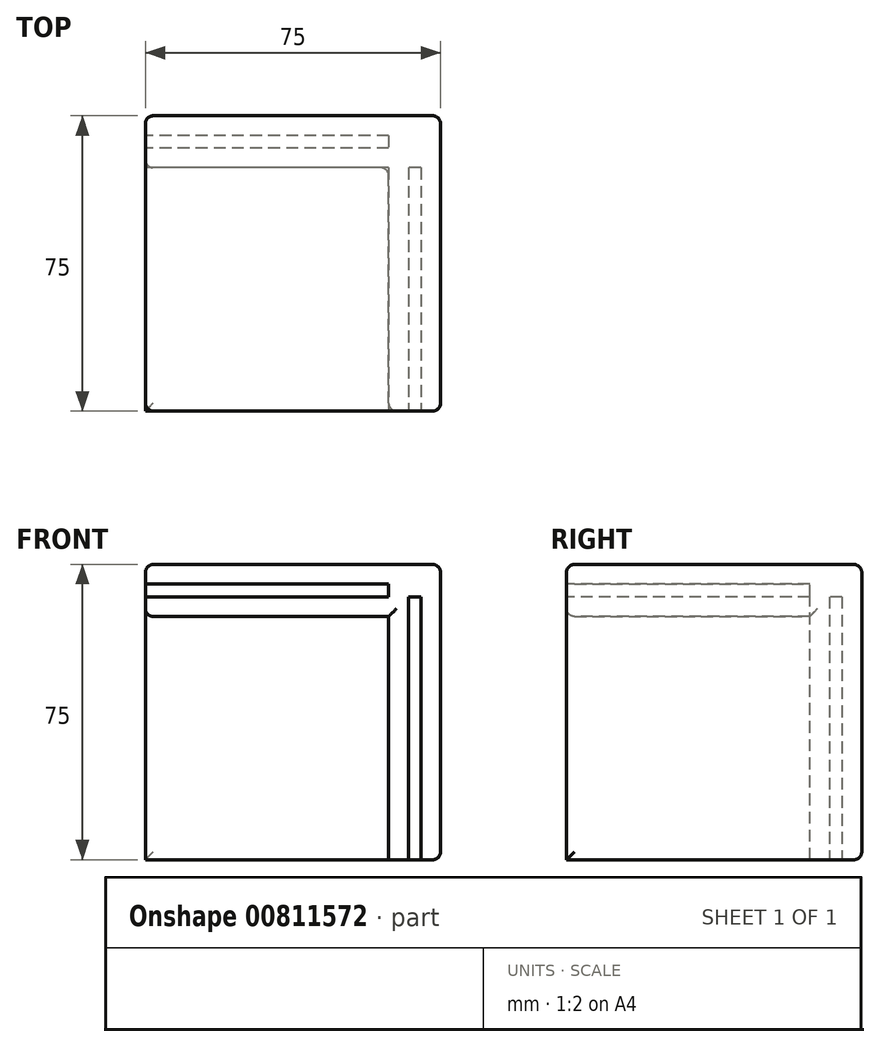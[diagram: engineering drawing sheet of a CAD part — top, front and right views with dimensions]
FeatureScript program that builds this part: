
annotation { "Feature Type Name" : "Feature", "Feature Type Description" : "" }
export const myFeature = defineFeature(function(context is Context, id is Id, definition is map)
    precondition{}
    {
        {
            var Q0;
            Q0=qCreatedBy(makeId("Top.planeOp"),FACE);
            var sketch = newSketch(context, id + "F0", { "sketchPlane" : qUnion([Q0])});
            skLineSegment(sketch, "E0.bottom", {"start": v(37.5, -37.5) * mm, "end": v(-37.5, -37.5) * mm});
            skLineSegment(sketch, "E0.top", {"start": v(37.5, 37.5) * mm, "end": v(-37.5, 37.5) * mm});
            skLineSegment(sketch, "E0.left", {"start": v(37.5, -37.5) * mm, "end": v(37.5, 37.5) * mm});
            skLineSegment(sketch, "E0.right", {"start": v(-37.5, -37.5) * mm, "end": v(-37.5, 37.5) * mm});
            skPoint(sketch, "E0.middle", {"position": v(0, 0) * mm});
            skSolve(sketch);
        }
        {
            var Q0;
            Q0=makeQuery(id+"F0.imprint","IMPRINT",FACE,{"disambiguationData":[TD([[makeQuery(id+"F0.imprint","IMPRINT",EDGE,{"derivedFrom":sQuery(id+"F0.wireOp",EDGE,"E0.bottom")}),-1.0]])]});
            extrude(context, id + "F1", {"entities" : qUnion([Q0]), "depth" : 5 * mm, "offsetDistance" : 25 * mm});
        }
        {
            var Q0;
            Q0=makeQuery(id+"F1.opExtrude","SWEPT_FACE",FACE,{"disambiguationData":[OSD([sQuery(id+"F0.wireOp",EDGE,"E0.right")])]});
            var sketch = newSketch(context, id + "F2", { "sketchPlane" : qUnion([Q0])});
            skLineSegment(sketch, "E1.bottom", {"start": v(-37.5, 5) * mm, "end": v(-32.5, 5) * mm});
            skLineSegment(sketch, "E1.top", {"start": v(-37.5, -70) * mm, "end": v(-32.5, -70) * mm});
            skLineSegment(sketch, "E1.left", {"start": v(-37.5, 5) * mm, "end": v(-37.5, -70) * mm});
            skLineSegment(sketch, "E1.right", {"start": v(-32.5, 5) * mm, "end": v(-32.5, -70) * mm});
            skLineSegment(sketch, "E2.bottom", {"start": v(-29.3, 5) * mm, "end": v(-24.3, 5) * mm});
            skLineSegment(sketch, "E2.top", {"start": v(-29.3, -70) * mm, "end": v(-24.3, -70) * mm});
            skLineSegment(sketch, "E2.left", {"start": v(-29.3, 5) * mm, "end": v(-29.3, -70) * mm});
            skLineSegment(sketch, "E2.right", {"start": v(-24.3, 5) * mm, "end": v(-24.3, -70) * mm});
            skSolve(sketch);
        }
        {
            var Q0;
            {var subQ0=sQuery(id+"F2.wireOp",EDGE,"E1.bottom");Q0=makeQuery(id+"F2.imprint","IMPRINT",FACE,{"disambiguationData":[TD([[makeQuery(id+"F2.imprint","IMPRINT",EDGE,{"derivedFrom":subQ0}),1.0]])]});}
            var Q1;
            {var subQ0=sQuery(id+"F2.wireOp",EDGE,"E2.bottom");Q1=makeQuery(id+"F2.imprint","IMPRINT",FACE,{"disambiguationData":[TD([[makeQuery(id+"F2.imprint","IMPRINT",EDGE,{"derivedFrom":subQ0}),1.0]])]});}
            var Q2;
            {var subQ0=sQuery(id+"F2.wireOp",EDGE,"E2.top");Q2=makeQuery(id+"F2.imprint","IMPRINT",FACE,{"disambiguationData":[TD([[makeQuery(id+"F2.imprint","IMPRINT",EDGE,{"derivedFrom":subQ0}),1.0]])]});}
            var Q3;
            {var subQ0=sQuery(id+"F2.wireOp",EDGE,"E1.top");Q3=makeQuery(id+"F2.imprint","IMPRINT",FACE,{"disambiguationData":[TD([[makeQuery(id+"F2.imprint","IMPRINT",EDGE,{"derivedFrom":subQ0}),1.0]])]});}
            var Q4;
            Q4=makeQuery(id+"F1.opExtrude","SWEPT_FACE",FACE,{"disambiguationData":[OSD([sQuery(id+"F0.wireOp",EDGE,"E0.left")])]});
            extrude(context, id + "F3", {"entities" : qUnion([Q0, Q1, Q2, Q3]), "operationType" : NewBodyOperationType.ADD, "endBound" : BoundingType.UP_TO_SURFACE, "oppositeDirection" : true, "depth" : 25 * mm, "endBoundEntityFace" : qUnion([Q4]), "offsetDistance" : 25 * mm});
        }
        {
            var Q0;
            Q0=makeQuery(id+"F1.opExtrude","SWEPT_FACE",FACE,{"disambiguationData":[OSD([sQuery(id+"F0.wireOp",EDGE,"E0.bottom")])]});
            var sketch = newSketch(context, id + "F4", { "sketchPlane" : qUnion([Q0])});
            skLineSegment(sketch, "E3.bottom", {"start": v(37.5, 5) * mm, "end": v(32.5, 5) * mm});
            skLineSegment(sketch, "E3.top", {"start": v(37.5, -70) * mm, "end": v(32.5, -70) * mm});
            skLineSegment(sketch, "E3.left", {"start": v(37.5, 5) * mm, "end": v(37.5, -70) * mm});
            skLineSegment(sketch, "E3.right", {"start": v(32.5, 5) * mm, "end": v(32.5, -70) * mm});
            skLineSegment(sketch, "E4.bottom", {"start": v(29.3, 5) * mm, "end": v(24.3, 5) * mm});
            skLineSegment(sketch, "E4.top", {"start": v(29.3, -70) * mm, "end": v(24.3, -70) * mm});
            skLineSegment(sketch, "E4.left", {"start": v(29.3, 5) * mm, "end": v(29.3, -70) * mm});
            skLineSegment(sketch, "E4.right", {"start": v(24.3, 5) * mm, "end": v(24.3, -70) * mm});
            skSolve(sketch);
        }
        {
            var Q0;
            Q0=qSketchRegion(id+"F4",true);
            var Q1;
            Q1=makeQuery(id+"F3.opExtrude","SWEPT_FACE",FACE,{"disambiguationData":[OSD([sQuery(id+"F2.wireOp",EDGE,"E1.right")])]});
            extrude(context, id + "F5", {"entities" : qUnion([Q0]), "operationType" : NewBodyOperationType.ADD, "endBound" : BoundingType.UP_TO_SURFACE, "oppositeDirection" : true, "depth" : 25 * mm, "endBoundEntityFace" : qUnion([Q1]), "offsetDistance" : 25 * mm});
        }
        {
            var Q0;
            {var subQ0=sQuery(id+"F2.wireOp",EDGE,"E1.right");var subQ1=makeQuery(id+"F3.opExtrude","SWEPT_FACE",FACE,{"disambiguationData":[OSD([subQ0])]});var subQ7=sQuery(id+"F0.wireOp",EDGE,"E0.right");var subQ8=sQuery(id+"F0.wireOp",EDGE,"E0.left");Q0=makeQuery(id+"F5.boolean.opBoolean","SPLIT",FACE,{"disambiguationData":[TD([makeQuery(id+"F5.opExtrude","SWEPT_FACE",FACE,{"disambiguationData":[OSD([sQuery(id+"F4.wireOp",EDGE,"E3.right")])]})])],"derivedFrom":makeQuery(id+"F3.boolean.opBoolean","SPLIT",FACE,{"disambiguationData":[TD([subQ1])],"derivedFrom":makeQuery(id+"F1.opExtrude","CAP_FACE",FACE,{"disambiguationData":[OSD([sQuery(id+"F0.wireOp",EDGE,"E0.bottom"),sQuery(id+"F0.wireOp",EDGE,"E0.top"),subQ8,subQ7])],"isStart":true})})});}
            var Q1;
            Q1=makeQuery(id+"F1.opExtrude","CAP_FACE",FACE,{"disambiguationData":[OSD([sQuery(id+"F0.wireOp",EDGE,"E0.bottom"),sQuery(id+"F0.wireOp",EDGE,"E0.top"),sQuery(id+"F0.wireOp",EDGE,"E0.left"),sQuery(id+"F0.wireOp",EDGE,"E0.right")])],"isStart":false});
            extrude(context, id + "F6", {"entities" : qUnion([Q0]), "operationType" : NewBodyOperationType.ADD, "endBound" : BoundingType.UP_TO_SURFACE, "oppositeDirection" : true, "depth" : 25 * mm, "endBoundEntityFace" : qUnion([Q1]), "offsetDistance" : 25 * mm});
        }
        {
            var Q0;
            Q0=makeQuery(id+"F5.boolean.opBoolean","MERGE",FACE,{"derivedFrom":[makeQuery(id+"F3.opExtrude","SWEPT_FACE",FACE,{"disambiguationData":[OSD([sQuery(id+"F2.wireOp",EDGE,"E1.top")])]}),makeQuery(id+"F3.opExtrude","SWEPT_FACE",FACE,{"disambiguationData":[OSD([sQuery(id+"F2.wireOp",EDGE,"E2.top")])]}),makeQuery(id+"F5.opExtrude","SWEPT_FACE",FACE,{"disambiguationData":[OSD([sQuery(id+"F4.wireOp",EDGE,"E3.top")])]}),makeQuery(id+"F5.opExtrude","SWEPT_FACE",FACE,{"disambiguationData":[OSD([sQuery(id+"F4.wireOp",EDGE,"E4.top")])]})]});
            var sketch = newSketch(context, id + "F7", { "sketchPlane" : qUnion([Q0])});
            skLineSegment(sketch, "E5.bottom", {"start": v(32.5, -29.3) * mm, "end": v(29.3, -29.3) * mm});
            skLineSegment(sketch, "E5.top", {"start": v(32.5, -32.5) * mm, "end": v(29.3, -32.5) * mm});
            skLineSegment(sketch, "E5.left", {"start": v(32.5, -29.3) * mm, "end": v(32.5, -32.5) * mm});
            skLineSegment(sketch, "E5.right", {"start": v(29.3, -29.3) * mm, "end": v(29.3, -32.5) * mm});
            skSolve(sketch);
        }
        {
            var Q0;
            Q0=qSketchRegion(id+"F7",true);
            var Q1;
            Q1=makeQuery(id+"F1.opExtrude","CAP_FACE",FACE,{"disambiguationData":[OSD([sQuery(id+"F0.wireOp",EDGE,"E0.bottom"),sQuery(id+"F0.wireOp",EDGE,"E0.top"),sQuery(id+"F0.wireOp",EDGE,"E0.left"),sQuery(id+"F0.wireOp",EDGE,"E0.right")])],"isStart":false});
            extrude(context, id + "F8", {"entities" : qUnion([Q0]), "operationType" : NewBodyOperationType.ADD, "endBound" : BoundingType.UP_TO_SURFACE, "oppositeDirection" : true, "depth" : 25 * mm, "endBoundEntityFace" : qUnion([Q1]), "offsetDistance" : 25 * mm});
        }
        {
            var Q0;
            Q0=makeQuery(id+"F3.boolean.opBoolean","MERGE",FACE,{"derivedFrom":[makeQuery(id+"F1.opExtrude","SWEPT_FACE",FACE,{"disambiguationData":[OSD([sQuery(id+"F0.wireOp",EDGE,"E0.right")])]}),makeQuery(id+"F3.opExtrude","CAP_FACE",FACE,{"disambiguationData":[OSD([sQuery(id+"F2.wireOp",EDGE,"E1.bottom"),sQuery(id+"F2.wireOp",EDGE,"E1.top"),sQuery(id+"F2.wireOp",EDGE,"E1.left"),sQuery(id+"F2.wireOp",EDGE,"E1.right")])],"isStart":true}),makeQuery(id+"F3.opExtrude","CAP_FACE",FACE,{"disambiguationData":[OSD([sQuery(id+"F2.wireOp",EDGE,"E2.bottom"),sQuery(id+"F2.wireOp",EDGE,"E2.top"),sQuery(id+"F2.wireOp",EDGE,"E2.left"),sQuery(id+"F2.wireOp",EDGE,"E2.right")])],"isStart":true})]});
            var sketch = newSketch(context, id + "F9", { "sketchPlane" : qUnion([Q0])});
            skLineSegment(sketch, "E6.bottom", {"start": v(-24.3, -3.2) * mm, "end": v(37.5, -3.2) * mm});
            skLineSegment(sketch, "E6.top", {"start": v(-24.3, -8.2) * mm, "end": v(37.5, -8.2) * mm});
            skLineSegment(sketch, "E6.left", {"start": v(-24.3, -3.2) * mm, "end": v(-24.3, -8.2) * mm});
            skLineSegment(sketch, "E6.right", {"start": v(37.5, -3.2) * mm, "end": v(37.5, -8.2) * mm});
            skLineSegment(sketch, "E7.0", {"start": v(37.5, 0) * mm, "end": v(37.5, -70) * mm});
            skSolve(sketch);
        }
        {
            var Q0;
            {var subQ0=sQuery(id+"F9.wireOp",EDGE,"E6.bottom");Q0=makeQuery(id+"F9.imprint","IMPRINT",FACE,{"disambiguationData":[TD([[makeQuery(id+"F9.imprint","IMPRINT",EDGE,{"derivedFrom":subQ0}),-1.0]])]});}
            var Q1;
            {var subQ1=sQuery(id+"F0.wireOp",EDGE,"E0.bottom");var subQ3=sQuery(id+"F4.wireOp",EDGE,"E4.right");Q1=makeQuery(id+"F5.boolean.opBoolean","SPLIT",FACE,{"disambiguationData":[TD([makeQuery(id+"F1.opExtrude","SWEPT_FACE",FACE,{"disambiguationData":[OSD([subQ1])]})])],"derivedFrom":makeQuery(id+"F5.opExtrude","SWEPT_FACE",FACE,{"disambiguationData":[OSD([subQ3])]})});}
            extrude(context, id + "F10", {"entities" : qUnion([Q0]), "operationType" : NewBodyOperationType.ADD, "endBound" : BoundingType.UP_TO_SURFACE, "oppositeDirection" : true, "depth" : 25 * mm, "endBoundEntityFace" : qUnion([Q1]), "offsetDistance" : 25 * mm});
        }
        {
            var Q0;
            Q0=makeQuery(id+"F1.opExtrude","CAP_FACE",FACE,{"disambiguationData":[OSD([sQuery(id+"F0.wireOp",EDGE,"E0.bottom"),sQuery(id+"F0.wireOp",EDGE,"E0.top"),sQuery(id+"F0.wireOp",EDGE,"E0.left"),sQuery(id+"F0.wireOp",EDGE,"E0.right")])],"isStart":false});
            var Q1;
            Q1=makeQuery(id+"F5.boolean.opBoolean","MERGE",FACE,{"derivedFrom":[makeQuery(id+"F3.boolean.opBoolean","MERGE",FACE,{"derivedFrom":[makeQuery(id+"F1.opExtrude","SWEPT_FACE",FACE,{"disambiguationData":[OSD([sQuery(id+"F0.wireOp",EDGE,"E0.left")])]}),makeQuery(id+"F3.opExtrude","CAP_FACE",FACE,{"disambiguationData":[OSD([sQuery(id+"F2.wireOp",EDGE,"E1.bottom"),sQuery(id+"F2.wireOp",EDGE,"E1.top"),sQuery(id+"F2.wireOp",EDGE,"E1.left"),sQuery(id+"F2.wireOp",EDGE,"E1.right")])],"isStart":false}),makeQuery(id+"F3.opExtrude","CAP_FACE",FACE,{"disambiguationData":[OSD([sQuery(id+"F2.wireOp",EDGE,"E2.bottom"),sQuery(id+"F2.wireOp",EDGE,"E2.top"),sQuery(id+"F2.wireOp",EDGE,"E2.left"),sQuery(id+"F2.wireOp",EDGE,"E2.right")])],"isStart":false})]}),makeQuery(id+"F5.opExtrude","SWEPT_FACE",FACE,{"disambiguationData":[OSD([sQuery(id+"F4.wireOp",EDGE,"E3.left")])]})]});
            var Q2;
            Q2=makeQuery(id+"F3.boolean.opBoolean","MERGE",FACE,{"derivedFrom":[makeQuery(id+"F1.opExtrude","SWEPT_FACE",FACE,{"disambiguationData":[OSD([sQuery(id+"F0.wireOp",EDGE,"E0.top")])]}),makeQuery(id+"F3.opExtrude","SWEPT_FACE",FACE,{"disambiguationData":[OSD([sQuery(id+"F2.wireOp",EDGE,"E1.left")])]})]});
            var Q3;
            Q3=makeQuery(id+"F10.opExtrude","CAP_EDGE",EDGE,{"disambiguationData":[OSD([sQuery(id+"F9.wireOp",EDGE,"E7.0")])],"isStart":true});
            var Q4;
            Q4=makeQuery(id+"F10.opExtrude","CAP_EDGE",EDGE,{"disambiguationData":[OSD([sQuery(id+"F9.wireOp",EDGE,"E6.top")])],"isStart":true});
            var Q5;
            {var subQ1=sQuery(id+"F2.wireOp",EDGE,"E2.right");var subQ3=sQuery(id+"F2.wireOp",EDGE,"E1.top");Q5=makeQuery(id+"F10.boolean.opBoolean","SPLIT",EDGE,{"disambiguationData":[TD([makeQuery(id+"F3.opExtrude","SWEPT_FACE",FACE,{"disambiguationData":[OSD([subQ3])]})])],"derivedFrom":makeQuery(id+"F3.opExtrude","CAP_EDGE",EDGE,{"disambiguationData":[OSD([subQ1])],"isStart":true})});}
            var Q6;
            {var subQ0=sQuery(id+"F4.wireOp",EDGE,"E4.right");Q6=makeQuery(id+"F10.boolean.opBoolean","SPLIT",EDGE,{"disambiguationData":[TD([makeQuery(id+"F3.opExtrude","SWEPT_FACE",FACE,{"disambiguationData":[OSD([sQuery(id+"F2.wireOp",EDGE,"E1.top")])]})])],"derivedFrom":makeQuery(id+"F5.opExtrude","CAP_EDGE",EDGE,{"disambiguationData":[OSD([subQ0])],"isStart":true})});}
            var Q7;
            Q7=makeQuery(id+"F10.opExtrude","SWEPT_EDGE",EDGE,{"disambiguationData":[OSD([sQuery(id+"F9.wireOp",EDGE,"E6.top"),sQuery(id+"F9.wireOp",EDGE,"E7.0")])]});
            var Q8;
            Q8=makeQuery(id+"F1.opExtrude","SWEPT_EDGE",EDGE,{"disambiguationData":[OSD([sQuery(id+"F0.wireOp",EDGE,"E0.bottom"),sQuery(id+"F0.wireOp",EDGE,"E0.right")])]});
            var Q9;
            {var subQ0=makeQuery(id+"F3.opExtrude","SWEPT_FACE",FACE,{"disambiguationData":[OSD([sQuery(id+"F2.wireOp",EDGE,"E2.right")])]});var subQ1=makeQuery(id+"F5.opExtrude","SWEPT_FACE",FACE,{"disambiguationData":[OSD([sQuery(id+"F4.wireOp",EDGE,"E4.right")])]});Q9=makeQuery(id+"F10.boolean.opBoolean","SPLIT",EDGE,{"disambiguationData":[TD([makeQuery(id+"F3.opExtrude","SWEPT_FACE",FACE,{"disambiguationData":[OSD([sQuery(id+"F2.wireOp",EDGE,"E1.top")])]})])],"derivedFrom":makeQuery(id+"F5.boolean.opBoolean","INTERSECT",EDGE,{"derivedFrom":[subQ0,subQ1]})});}
            fillet(context, id + "F11", {"entities" : qUnion([Q0, Q1, Q2, Q3, Q4, Q5, Q6, Q7, Q8, Q9]), "radius" : 2 * mm, "tangentPropagation" : true, "allowEdgeOverflow" : false});
        }
        {
            var Q0;
            Q0=makeQuery(id+"F10.boolean.opBoolean","MERGE",FACE,{"derivedFrom":[makeQuery(id+"F3.boolean.opBoolean","MERGE",FACE,{"derivedFrom":[makeQuery(id+"F1.opExtrude","SWEPT_FACE",FACE,{"disambiguationData":[OSD([sQuery(id+"F0.wireOp",EDGE,"E0.right")])]}),makeQuery(id+"F3.opExtrude","CAP_FACE",FACE,{"disambiguationData":[OSD([sQuery(id+"F2.wireOp",EDGE,"E1.bottom"),sQuery(id+"F2.wireOp",EDGE,"E1.top"),sQuery(id+"F2.wireOp",EDGE,"E1.left"),sQuery(id+"F2.wireOp",EDGE,"E1.right")])],"isStart":true}),makeQuery(id+"F3.opExtrude","CAP_FACE",FACE,{"disambiguationData":[OSD([sQuery(id+"F2.wireOp",EDGE,"E2.bottom"),sQuery(id+"F2.wireOp",EDGE,"E2.top"),sQuery(id+"F2.wireOp",EDGE,"E2.left"),sQuery(id+"F2.wireOp",EDGE,"E2.right")])],"isStart":true})]}),makeQuery(id+"F10.opExtrude","CAP_FACE",FACE,{"disambiguationData":[OSD([sQuery(id+"F9.wireOp",EDGE,"E6.bottom"),sQuery(id+"F9.wireOp",EDGE,"E6.top"),sQuery(id+"F9.wireOp",EDGE,"E6.left"),sQuery(id+"F9.wireOp",EDGE,"E7.0")])],"isStart":true})]});
            var sketch = newSketch(context, id + "F12", { "sketchPlane" : qUnion([Q0])});
            skLineSegment(sketch, "E8.bottom", {"start": v(-32.5, 0) * mm, "end": v(-29.3, 0) * mm});
            skLineSegment(sketch, "E8.top", {"start": v(-32.5, -3.2) * mm, "end": v(-29.3, -3.2) * mm});
            skLineSegment(sketch, "E8.left", {"start": v(-32.5, 0) * mm, "end": v(-32.5, -3.2) * mm});
            skLineSegment(sketch, "E8.right", {"start": v(-29.3, 0) * mm, "end": v(-29.3, -3.2) * mm});
            skSolve(sketch);
        }
        {
            var Q0;
            Q0 = qSketchRegion(id + "F12", true);
            var Q1;
            Q1=makeQuery(id+"F5.boolean.opBoolean","MERGE",FACE,{"derivedFrom":[makeQuery(id+"F3.boolean.opBoolean","MERGE",FACE,{"derivedFrom":[makeQuery(id+"F1.opExtrude","SWEPT_FACE",FACE,{"disambiguationData":[OSD([sQuery(id+"F0.wireOp",EDGE,"E0.left")])]}),makeQuery(id+"F3.opExtrude","CAP_FACE",FACE,{"disambiguationData":[OSD([sQuery(id+"F2.wireOp",EDGE,"E1.bottom"),sQuery(id+"F2.wireOp",EDGE,"E1.top"),sQuery(id+"F2.wireOp",EDGE,"E1.left"),sQuery(id+"F2.wireOp",EDGE,"E1.right")])],"isStart":false}),makeQuery(id+"F3.opExtrude","CAP_FACE",FACE,{"disambiguationData":[OSD([sQuery(id+"F2.wireOp",EDGE,"E2.bottom"),sQuery(id+"F2.wireOp",EDGE,"E2.top"),sQuery(id+"F2.wireOp",EDGE,"E2.left"),sQuery(id+"F2.wireOp",EDGE,"E2.right")])],"isStart":false})]}),makeQuery(id+"F5.opExtrude","SWEPT_FACE",FACE,{"disambiguationData":[OSD([sQuery(id+"F4.wireOp",EDGE,"E3.left")])]})]});
            extrude(context, id + "F13", {"entities" : qUnion([Q0]), "operationType" : NewBodyOperationType.ADD, "endBound" : BoundingType.UP_TO_SURFACE, "oppositeDirection" : true, "depth" : 25 * mm, "endBoundEntityFace" : qUnion([Q1]), "offsetDistance" : 25 * mm});
        }
        {
            var Q0;
            Q0=makeQuery(id+"F10.boolean.opBoolean","MERGE",FACE,{"derivedFrom":[makeQuery(id+"F5.boolean.opBoolean","MERGE",FACE,{"derivedFrom":[makeQuery(id+"F1.opExtrude","SWEPT_FACE",FACE,{"disambiguationData":[OSD([sQuery(id+"F0.wireOp",EDGE,"E0.bottom")])]}),makeQuery(id+"F5.opExtrude","CAP_FACE",FACE,{"disambiguationData":[OSD([sQuery(id+"F4.wireOp",EDGE,"E3.bottom"),sQuery(id+"F4.wireOp",EDGE,"E3.top"),sQuery(id+"F4.wireOp",EDGE,"E3.left"),sQuery(id+"F4.wireOp",EDGE,"E3.right")])],"isStart":true}),makeQuery(id+"F5.opExtrude","CAP_FACE",FACE,{"disambiguationData":[OSD([sQuery(id+"F4.wireOp",EDGE,"E4.bottom"),sQuery(id+"F4.wireOp",EDGE,"E4.top"),sQuery(id+"F4.wireOp",EDGE,"E4.left"),sQuery(id+"F4.wireOp",EDGE,"E4.right")])],"isStart":true})]}),makeQuery(id+"F10.opExtrude","SWEPT_FACE",FACE,{"disambiguationData":[OSD([sQuery(id+"F9.wireOp",EDGE,"E7.0")])]})]});
            var sketch = newSketch(context, id + "F14", { "sketchPlane" : qUnion([Q0])});
            skLineSegment(sketch, "E9.bottom", {"start": v(29.3, 0) * mm, "end": v(32.5, 0) * mm});
            skLineSegment(sketch, "E9.top", {"start": v(29.3, -3.2) * mm, "end": v(32.5, -3.2) * mm});
            skLineSegment(sketch, "E9.left", {"start": v(29.3, 0) * mm, "end": v(29.3, -3.2) * mm});
            skLineSegment(sketch, "E9.right", {"start": v(32.5, 0) * mm, "end": v(32.5, -3.2) * mm});
            skSolve(sketch);
        }
        {
            var Q0;
            Q0=makeQuery(id+"F14.imprint","IMPRINT",FACE,{"disambiguationData":[TD([[makeQuery(id+"F14.imprint","IMPRINT",EDGE,{"derivedFrom":sQuery(id+"F14.wireOp",EDGE,"E9.bottom")}),1.0]])]});
            var Q1;
            Q1=makeQuery(id+"F3.boolean.opBoolean","MERGE",FACE,{"derivedFrom":[makeQuery(id+"F1.opExtrude","SWEPT_FACE",FACE,{"disambiguationData":[OSD([sQuery(id+"F0.wireOp",EDGE,"E0.top")])]}),makeQuery(id+"F3.opExtrude","SWEPT_FACE",FACE,{"disambiguationData":[OSD([sQuery(id+"F2.wireOp",EDGE,"E1.left")])]})]});
            extrude(context, id + "F15", {"entities" : qUnion([Q0]), "operationType" : NewBodyOperationType.ADD, "endBound" : BoundingType.UP_TO_SURFACE, "oppositeDirection" : true, "depth" : 25 * mm, "endBoundEntityFace" : qUnion([Q1]), "offsetDistance" : 25 * mm});
        }
    });
